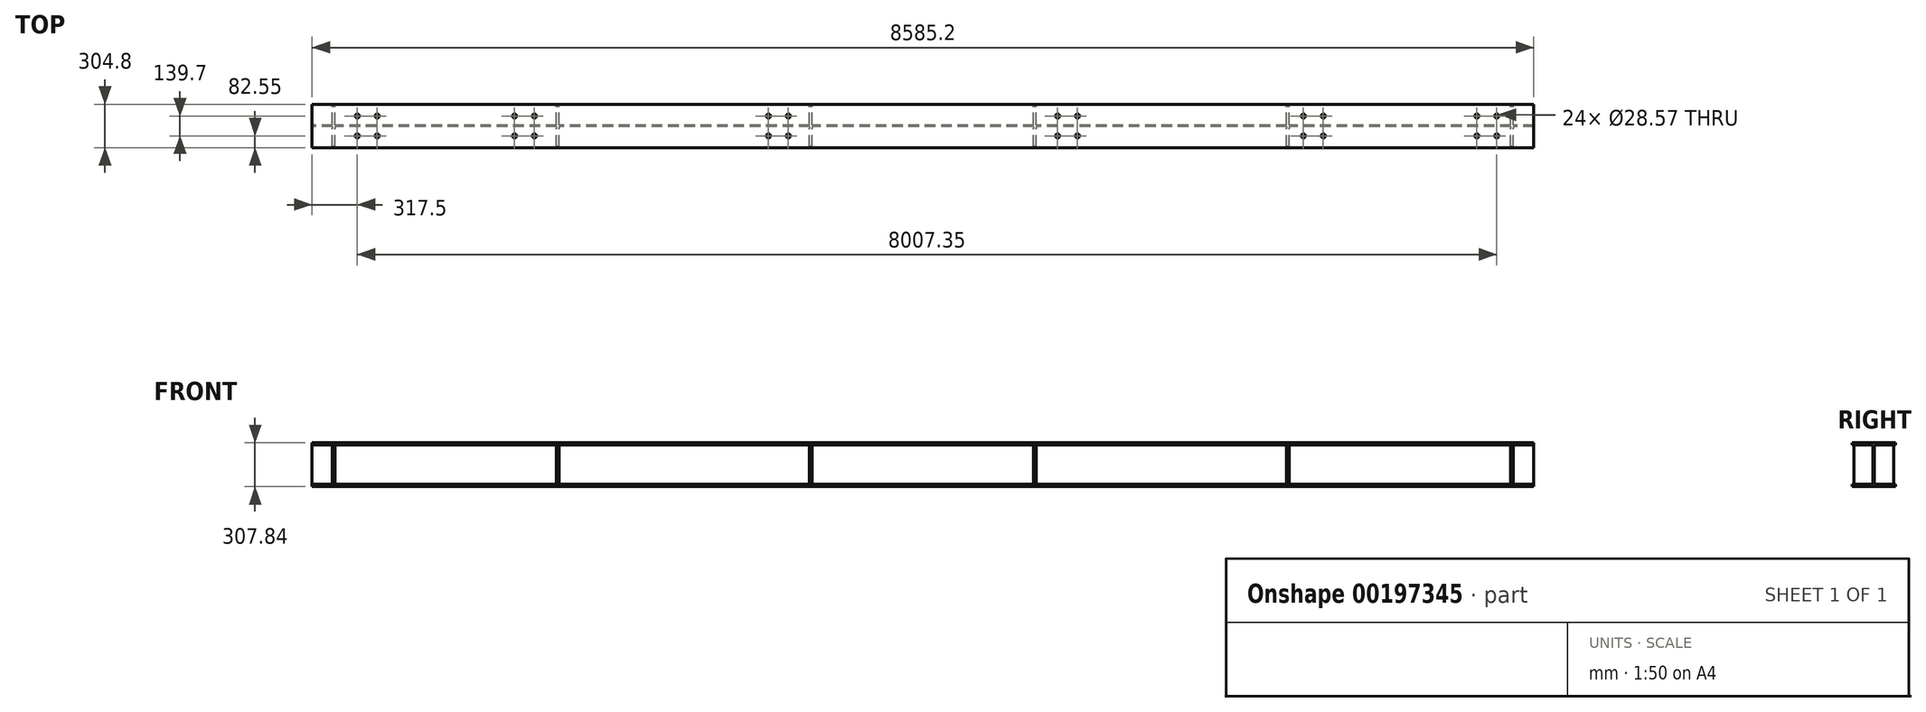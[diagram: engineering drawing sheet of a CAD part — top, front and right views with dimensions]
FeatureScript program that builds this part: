
annotation { "Feature Type Name" : "Feature", "Feature Type Description" : "" }
export const myFeature = defineFeature(function(context is Context, id is Id, definition is map)
    precondition{}
    {
        {
            var Q0;
            Q0=qCreatedBy(makeId("Right.planeOp"),FACE);
            var sketch = newSketch(context, id + "F0", { "sketchPlane" : qUnion([Q0])});
            skLineSegment(sketch, "E0.bottom", {"start": v(-152.4, 153.92) * mm, "end": v(152.4, 153.92) * mm});
            skLineSegment(sketch, "E0.top", {"start": v(-152.4, -153.92) * mm, "end": v(152.4, -153.92) * mm});
            skLineSegment(sketch, "E0.left", {"start": v(-152.4, 153.92) * mm, "end": v(-152.4, 138.56) * mm});
            skLineSegment(sketch, "E0.right", {"start": v(152.4, 153.92) * mm, "end": v(152.4, 138.56) * mm});
            skPoint(sketch, "E0.middle", {"position": v(0, 0) * mm});
            skLineSegment(sketch, "E1.0", {"start": v(-152.4, 138.56) * mm, "end": v(-17.65, 138.56) * mm});
            skLineSegment(sketch, "E2.0", {"start": v(-152.4, -138.56) * mm, "end": v(-17.65, -138.56) * mm});
            skLineSegment(sketch, "E3", {"start": v(0, 174.3) * mm, "end": v(0, -181.52) * mm, "construction": true});
            skLineSegment(sketch, "E4.0", {"start": v(-4.95, 125.86) * mm, "end": v(-4.95, -125.86) * mm});
            skLineSegment(sketch, "E5.MirrorCS", {"start": v(4.95, 125.86) * mm, "end": v(4.95, -125.86) * mm});
            skPoint(sketch, "E6.orphan", {"position": v(-4.95, 174.3) * mm});
            skPoint(sketch, "E7.orphan", {"position": v(4.95, 174.3) * mm});
            skLineSegment(sketch, "E8.trimOffspring", {"start": v(17.65, 138.56) * mm, "end": v(152.4, 138.56) * mm});
            skLineSegment(sketch, "E9.trimOffspring", {"start": v(4.95, -153.92) * mm, "end": v(4.95, -181.52) * mm});
            skLineSegment(sketch, "E10.trimOffspring", {"start": v(-4.95, -153.92) * mm, "end": v(-4.95, -181.52) * mm});
            skLineSegment(sketch, "E11.trimOffspring", {"start": v(17.65, -138.56) * mm, "end": v(152.4, -138.56) * mm});
            skLineSegment(sketch, "E12.trimOffspring", {"start": v(-152.4, -138.56) * mm, "end": v(-152.4, -153.92) * mm});
            skLineSegment(sketch, "E13.trimOffspring", {"start": v(152.4, -138.56) * mm, "end": v(152.4, -153.92) * mm});
            skPoint(sketch, "E14.visualSharp", {"position": v(-4.95, 138.56) * mm});
            skArc(sketch, "E14.filletArc", {"start": v(-4.95, 125.86) * mm, "mid": v(-8.67, 134.84) * mm, "end": v(-17.65, 138.56) * mm});
            skPoint(sketch, "E15.visualSharp", {"position": v(4.95, 138.56) * mm});
            skArc(sketch, "E15.filletArc", {"start": v(17.65, 138.56) * mm, "mid": v(8.67, 134.84) * mm, "end": v(4.95, 125.86) * mm});
            skPoint(sketch, "E16.visualSharp", {"position": v(-4.95, -138.56) * mm});
            skArc(sketch, "E16.filletArc", {"start": v(-17.65, -138.56) * mm, "mid": v(-8.67, -134.84) * mm, "end": v(-4.95, -125.86) * mm});
            skPoint(sketch, "E17.visualSharp", {"position": v(4.95, -138.56) * mm});
            skArc(sketch, "E17.filletArc", {"start": v(4.95, -125.86) * mm, "mid": v(8.67, -134.84) * mm, "end": v(17.65, -138.56) * mm});
            skSolve(sketch);
        }
        {
            var Q0;
            Q0 = qSketchRegion(id + "F0", true);
            extrude(context, id + "F1", {"entities" : qUnion([Q0]), "endBound" : BoundingType.SYMMETRIC, "depth" : 8585.2 * mm});
        }
        {
            var Q0;
            Q0=qCreatedBy(makeId("Front.planeOp"),FACE);
            var sketch = newSketch(context, id + "F2", { "sketchPlane" : qUnion([Q0])});
            skLineSegment(sketch, "E18.0", {"start": v(-4292.6, 502.23) * mm, "end": v(-4292.6, -566.62) * mm, "construction": true});
            skPoint(sketch, "E19.orphan", {"position": v(-4292.6, 125.86) * mm});
            skPoint(sketch, "E20.orphan", {"position": v(-4292.6, -125.86) * mm});
            skLineSegment(sketch, "E21.0", {"start": v(-4149.85, 502.23) * mm, "end": v(-4149.85, -566.62) * mm, "construction": true});
            skLineSegment(sketch, "E22.0", {"start": v(-2575.05, 502.23) * mm, "end": v(-2575.05, -566.62) * mm, "construction": true});
            skLineSegment(sketch, "E23.0", {"start": v(-797.05, 502.23) * mm, "end": v(-797.05, -566.62) * mm, "construction": true});
            skLineSegment(sketch, "E24.0", {"start": v(777.75, 502.23) * mm, "end": v(777.75, -566.62) * mm, "construction": true});
            skLineSegment(sketch, "E25.0", {"start": v(2555.75, 502.23) * mm, "end": v(2555.75, -566.62) * mm, "construction": true});
            skLineSegment(sketch, "E26.0", {"start": v(4130.55, 502.23) * mm, "end": v(4130.55, -566.62) * mm, "construction": true});
            skLineSegment(sketch, "E27.0", {"start": v(4292.6, 138.56) * mm, "end": v(-4292.6, 138.56) * mm, "construction": true});
            skLineSegment(sketch, "E28.0", {"start": v(4292.6, -138.56) * mm, "end": v(-4292.6, -138.56) * mm, "construction": true});
            skLineSegment(sketch, "E29.bottom", {"start": v(-4149.85, 138.56) * mm, "end": v(-4130.8, 138.56) * mm});
            skLineSegment(sketch, "E29.top", {"start": v(-4149.85, -138.56) * mm, "end": v(-4130.8, -138.56) * mm});
            skLineSegment(sketch, "E29.left", {"start": v(-4149.85, 138.56) * mm, "end": v(-4149.85, -138.56) * mm});
            skLineSegment(sketch, "E29.right", {"start": v(-4130.8, 138.56) * mm, "end": v(-4130.8, -138.56) * mm});
            skLineSegment(sketch, "E30.bottom", {"start": v(-2575.05, 138.56) * mm, "end": v(-2556, 138.56) * mm});
            skLineSegment(sketch, "E30.top", {"start": v(-2575.05, -138.56) * mm, "end": v(-2556, -138.56) * mm});
            skLineSegment(sketch, "E30.left", {"start": v(-2575.05, 138.56) * mm, "end": v(-2575.05, -138.56) * mm});
            skLineSegment(sketch, "E30.right", {"start": v(-2556, 138.56) * mm, "end": v(-2556, -138.56) * mm});
            skLineSegment(sketch, "E31.bottom", {"start": v(-797.05, 138.56) * mm, "end": v(-778, 138.56) * mm});
            skLineSegment(sketch, "E31.top", {"start": v(-797.05, -138.56) * mm, "end": v(-778, -138.56) * mm});
            skLineSegment(sketch, "E31.left", {"start": v(-797.05, 138.56) * mm, "end": v(-797.05, -138.56) * mm});
            skLineSegment(sketch, "E31.right", {"start": v(-778, 138.56) * mm, "end": v(-778, -138.56) * mm});
            skLineSegment(sketch, "E32.bottom", {"start": v(777.75, 138.56) * mm, "end": v(796.8, 138.56) * mm});
            skLineSegment(sketch, "E32.top", {"start": v(777.75, -138.56) * mm, "end": v(796.8, -138.56) * mm});
            skLineSegment(sketch, "E32.left", {"start": v(777.75, 138.56) * mm, "end": v(777.75, -138.56) * mm});
            skLineSegment(sketch, "E32.right", {"start": v(796.8, 138.56) * mm, "end": v(796.8, -138.56) * mm});
            skLineSegment(sketch, "E33.bottom", {"start": v(2555.75, 138.56) * mm, "end": v(2574.8, 138.56) * mm});
            skLineSegment(sketch, "E33.top", {"start": v(2555.75, -138.56) * mm, "end": v(2574.8, -138.56) * mm});
            skLineSegment(sketch, "E33.left", {"start": v(2555.75, 138.56) * mm, "end": v(2555.75, -138.56) * mm});
            skLineSegment(sketch, "E33.right", {"start": v(2574.8, 138.56) * mm, "end": v(2574.8, -138.56) * mm});
            skLineSegment(sketch, "E34.bottom", {"start": v(4130.55, 138.56) * mm, "end": v(4149.6, 138.56) * mm});
            skLineSegment(sketch, "E34.top", {"start": v(4130.55, -138.56) * mm, "end": v(4149.6, -138.56) * mm});
            skLineSegment(sketch, "E34.left", {"start": v(4130.55, 138.56) * mm, "end": v(4130.55, -138.56) * mm});
            skLineSegment(sketch, "E34.right", {"start": v(4149.6, 138.56) * mm, "end": v(4149.6, -138.56) * mm});
            skSolve(sketch);
        }
        {
            var Q0;
            Q0 = qSketchRegion(id + "F2", true);
            extrude(context, id + "F3", {"entities" : qUnion([Q0]), "operationType" : NewBodyOperationType.ADD, "endBound" : BoundingType.SYMMETRIC, "depth" : 279.4 * mm});
        }
        {
            var Q0;
            Q0=makeQuery(id+"F1.opExtrude","SWEPT_FACE",FACE,{"disambiguationData":[OSD([sQuery(id+"F0.wireOp",EDGE,"E0.bottom")])]});
            var sketch = newSketch(context, id + "F4", { "sketchPlane" : qUnion([Q0])});
            skLineSegment(sketch, "E35", {"start": v(-4949.1, 0) * mm, "end": v(4779.36, 0) * mm, "construction": true});
            skLineSegment(sketch, "E36.0", {"start": v(-4292.6, -665.82) * mm, "end": v(-4292.6, 694.01) * mm, "construction": true});
            skPoint(sketch, "E37.orphan", {"position": v(-4292.6, 152.4) * mm});
            skPoint(sketch, "E38.orphan", {"position": v(-4292.6, -152.4) * mm});
            skLineSegment(sketch, "E39.0", {"start": v(-3905.25, -665.82) * mm, "end": v(-3905.25, 694.01) * mm, "construction": true});
            skLineSegment(sketch, "E40.0", {"start": v(-2800.35, -665.82) * mm, "end": v(-2800.35, 694.01) * mm, "construction": true});
            skLineSegment(sketch, "E41.0", {"start": v(-1016, -665.82) * mm, "end": v(-1016, 694.01) * mm, "construction": true});
            skLineSegment(sketch, "E42.0", {"start": v(1016, -665.82) * mm, "end": v(1016, 694.01) * mm, "construction": true});
            skLineSegment(sketch, "E43.0", {"start": v(2743.2, -665.82) * mm, "end": v(2743.2, 694.01) * mm, "construction": true});
            skLineSegment(sketch, "E44.0", {"start": v(3962.4, -665.82) * mm, "end": v(3962.4, 694.01) * mm, "construction": true});
            skLineSegment(sketch, "E45.0", {"start": v(-4949.1, -69.85) * mm, "end": v(4779.36, -69.85) * mm, "construction": true});
            skLineSegment(sketch, "E46.MirrorCS", {"start": v(-4949.1, 69.85) * mm, "end": v(4779.36, 69.85) * mm, "construction": true});
            skLineSegment(sketch, "E47.0", {"start": v(-3975.1, -665.82) * mm, "end": v(-3975.1, 694.01) * mm, "construction": true});
            skLineSegment(sketch, "E48.MirrorCS", {"start": v(-3835.4, -665.82) * mm, "end": v(-3835.4, 694.01) * mm, "construction": true});
            skPoint(sketch, "E49", {"position": v(-3975.1, 69.85) * mm});
            skPoint(sketch, "E50", {"position": v(-3975.1, -69.85) * mm});
            skPoint(sketch, "E51", {"position": v(-3835.4, 69.85) * mm});
            skPoint(sketch, "E52", {"position": v(-3835.4, -69.85) * mm});
            skPoint(sketch, "E53.1.0.0", {"position": v(-2730.5, -69.85) * mm});
            skPoint(sketch, "E53.1.0.1", {"position": v(-2870.2, 69.85) * mm});
            skPoint(sketch, "E53.1.0.2", {"position": v(-2870.2, -69.85) * mm});
            skPoint(sketch, "E53.1.0.3", {"position": v(-2730.5, 69.85) * mm});
            skLineSegment(sketch, "E53.direction1", {"start": v(-3975.1, -69.85) * mm, "end": v(-2870.2, -69.85) * mm, "construction": true});
            skPoint(sketch, "E54.1.0.1", {"position": v(-1085.85, 69.85) * mm});
            skPoint(sketch, "E54.1.0.2", {"position": v(-946.15, -69.85) * mm});
            skPoint(sketch, "E54.1.0.3", {"position": v(-946.15, 69.85) * mm});
            skPoint(sketch, "E54.1.0.4", {"position": v(-1085.85, -69.85) * mm});
            skLineSegment(sketch, "E54.direction1", {"start": v(-2870.2, -69.85) * mm, "end": v(-1085.85, -69.85) * mm, "construction": true});
            skPoint(sketch, "E55.1.0.0", {"position": v(1085.85, -69.85) * mm});
            skPoint(sketch, "E55.1.0.1", {"position": v(946.15, 69.85) * mm});
            skPoint(sketch, "E55.1.0.2", {"position": v(1085.85, 69.85) * mm});
            skPoint(sketch, "E55.1.0.3", {"position": v(946.15, -69.85) * mm});
            skLineSegment(sketch, "E55.direction1", {"start": v(-1085.85, -69.85) * mm, "end": v(946.15, -69.85) * mm, "construction": true});
            skPoint(sketch, "E56.1.0.0", {"position": v(2673.35, -69.85) * mm});
            skPoint(sketch, "E56.1.0.1", {"position": v(2673.35, 69.85) * mm});
            skPoint(sketch, "E56.1.0.2", {"position": v(2813.05, 69.85) * mm});
            skPoint(sketch, "E56.1.0.3", {"position": v(2813.05, -69.85) * mm});
            skLineSegment(sketch, "E56.direction1", {"start": v(946.15, -69.85) * mm, "end": v(2673.35, -69.85) * mm, "construction": true});
            skPoint(sketch, "E57.1.0.0", {"position": v(3892.55, 69.85) * mm});
            skPoint(sketch, "E57.1.0.1", {"position": v(4032.25, -69.85) * mm});
            skPoint(sketch, "E57.1.0.2", {"position": v(4032.25, 69.85) * mm});
            skPoint(sketch, "E57.1.0.3", {"position": v(3892.55, -69.85) * mm});
            skLineSegment(sketch, "E57.direction1", {"start": v(2673.35, -69.85) * mm, "end": v(3892.55, -69.85) * mm, "construction": true});
            skSolve(sketch);
        }
        {
            var Q0;
            Q0=sQuery(id+"F4.wireOp",VERTEX,"E49");
            var Q1;
            Q1=sQuery(id+"F4.wireOp",VERTEX,"E51");
            var Q2;
            Q2=sQuery(id+"F4.wireOp",VERTEX,"E52");
            var Q3;
            Q3=sQuery(id+"F4.wireOp",VERTEX,"E50");
            var Q4;
            Q4=sQuery(id+"F4.wireOp",VERTEX,"E53.1.0.1");
            var Q5;
            Q5=sQuery(id+"F4.wireOp",VERTEX,"E53.1.0.3");
            var Q6;
            Q6=sQuery(id+"F4.wireOp",VERTEX,"E53.1.0.2");
            var Q7;
            Q7=sQuery(id+"F4.wireOp",VERTEX,"E53.1.0.0");
            var Q8;
            Q8=sQuery(id+"F4.wireOp",VERTEX,"E54.1.0.1");
            var Q9;
            Q9=sQuery(id+"F4.wireOp",VERTEX,"E54.1.0.3");
            var Q10;
            Q10=sQuery(id+"F4.wireOp",VERTEX,"E54.1.0.4");
            var Q11;
            Q11=sQuery(id+"F4.wireOp",VERTEX,"E54.1.0.2");
            var Q12;
            Q12=sQuery(id+"F4.wireOp",VERTEX,"E55.1.0.1");
            var Q13;
            Q13=sQuery(id+"F4.wireOp",VERTEX,"E55.1.0.2");
            var Q14;
            Q14=sQuery(id+"F4.wireOp",VERTEX,"E55.1.0.3");
            var Q15;
            Q15=sQuery(id+"F4.wireOp",VERTEX,"E55.1.0.0");
            var Q16;
            Q16=sQuery(id+"F4.wireOp",VERTEX,"E56.1.0.1");
            var Q17;
            Q17=sQuery(id+"F4.wireOp",VERTEX,"E56.1.0.2");
            var Q18;
            Q18=sQuery(id+"F4.wireOp",VERTEX,"E56.1.0.0");
            var Q19;
            Q19=sQuery(id+"F4.wireOp",VERTEX,"E56.1.0.3");
            var Q20;
            Q20=sQuery(id+"F4.wireOp",VERTEX,"E57.1.0.0");
            var Q21;
            Q21=sQuery(id+"F4.wireOp",VERTEX,"E57.1.0.2");
            var Q22;
            Q22=sQuery(id+"F4.wireOp",VERTEX,"E57.1.0.3");
            var Q23;
            Q23=sQuery(id+"F4.wireOp",VERTEX,"E57.1.0.1");
            var Q24;
            Q24=sQuery(id+"F4.wireOp",VERTEX,"E57.1.0.2");
            var Q25;
            Q25=makeQuery(id+"F1.opExtrude","SWEPT_BODY",BODY,{"disambiguationData":[OSD([sQuery(id+"F0.wireOp",EDGE,"E0.bottom"),sQuery(id+"F0.wireOp",EDGE,"E0.top"),sQuery(id+"F0.wireOp",EDGE,"E0.left"),sQuery(id+"F0.wireOp",EDGE,"E0.right"),sQuery(id+"F0.wireOp",EDGE,"E1.0"),sQuery(id+"F0.wireOp",EDGE,"E2.0"),sQuery(id+"F0.wireOp",EDGE,"E4.0"),sQuery(id+"F0.wireOp",EDGE,"E5.MirrorCS"),sQuery(id+"F0.wireOp",EDGE,"E8.trimOffspring"),sQuery(id+"F0.wireOp",EDGE,"E11.trimOffspring"),sQuery(id+"F0.wireOp",EDGE,"E12.trimOffspring"),sQuery(id+"F0.wireOp",EDGE,"E13.trimOffspring"),sQuery(id+"F0.wireOp",EDGE,"E14.filletArc"),sQuery(id+"F0.wireOp",EDGE,"E15.filletArc"),sQuery(id+"F0.wireOp",EDGE,"E16.filletArc"),sQuery(id+"F0.wireOp",EDGE,"E17.filletArc")])]});
            hole(context, id + "F5", {"style" : HoleStyle.SIMPLE, "endStyle" : HoleEndStyle.BLIND, "holeDiameter" : 28.57 * mm, "holeDepth" : 50.8 * mm, "locations" : qUnion([Q0, Q1, Q2, Q3, Q4, Q5, Q6, Q7, Q8, Q9, Q10, Q11, Q12, Q13, Q14, Q15, Q16, Q17, Q18, Q19, Q20, Q21, Q22, Q23, Q24]), "scope" : qUnion([Q25])});
        }
    });
